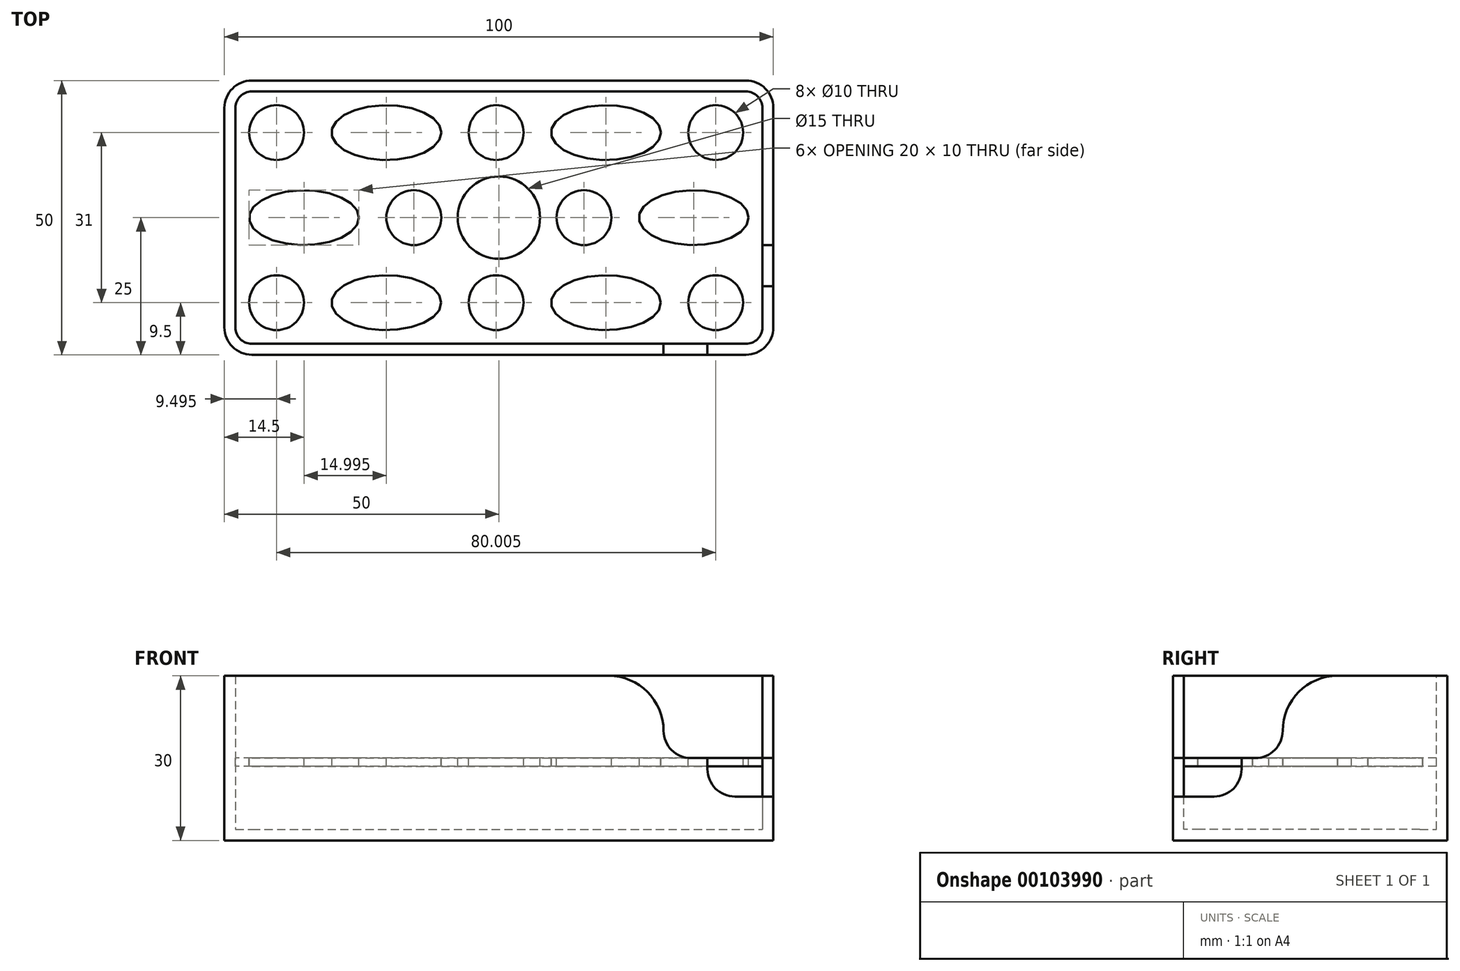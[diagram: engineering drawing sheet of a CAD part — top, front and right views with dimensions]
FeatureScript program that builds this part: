
annotation { "Feature Type Name" : "Feature", "Feature Type Description" : "" }
export const myFeature = defineFeature(function(context is Context, id is Id, definition is map)
    precondition{}
    {
        {
            var Q0;
            Q0=qCreatedBy(makeId("Top.planeOp"),FACE);
            var sketch = newSketch(context, id + "F0", { "sketchPlane" : qUnion([Q0])});
            skLineSegment(sketch, "E0.bottom", {"start": v(-50, 25) * mm, "end": v(50, 25) * mm});
            skLineSegment(sketch, "E0.top", {"start": v(-50, -25) * mm, "end": v(50, -25) * mm});
            skLineSegment(sketch, "E0.left", {"start": v(-50, 25) * mm, "end": v(-50, -25) * mm});
            skLineSegment(sketch, "E0.right", {"start": v(50, 25) * mm, "end": v(50, -25) * mm});
            skSolve(sketch);
        }
        {
            var Q0;
            Q0=makeQuery(id+"F0.imprint","IMPRINT",FACE,{"disambiguationData":[TD([[makeQuery(id+"F0.imprint","IMPRINT",EDGE,{"derivedFrom":sQuery(id+"F0.wireOp",EDGE,"E0.bottom")}),-1.0]])]});
            extrude(context, id + "F1", {"entities" : qUnion([Q0]), "depth" : 30 * mm});
        }
        {
            var Q0;
            Q0=makeQuery(id+"F1.opExtrude","SWEPT_EDGE",EDGE,{"disambiguationData":[OSD([sQuery(id+"F0.wireOp",EDGE,"E0.top"),sQuery(id+"F0.wireOp",EDGE,"E0.right")])]});
            var Q1;
            Q1=makeQuery(id+"F1.opExtrude","SWEPT_EDGE",EDGE,{"disambiguationData":[OSD([sQuery(id+"F0.wireOp",EDGE,"E0.bottom"),sQuery(id+"F0.wireOp",EDGE,"E0.right")])]});
            var Q2;
            Q2=makeQuery(id+"F1.opExtrude","SWEPT_EDGE",EDGE,{"disambiguationData":[OSD([sQuery(id+"F0.wireOp",EDGE,"E0.top"),sQuery(id+"F0.wireOp",EDGE,"E0.left")])]});
            var Q3;
            Q3=makeQuery(id+"F1.opExtrude","SWEPT_EDGE",EDGE,{"disambiguationData":[OSD([sQuery(id+"F0.wireOp",EDGE,"E0.bottom"),sQuery(id+"F0.wireOp",EDGE,"E0.left")])]});
            fillet(context, id + "F2", {"entities" : qUnion([Q0, Q1, Q2, Q3]), "radius" : 5 * mm, "tangentPropagation" : true, "allowEdgeOverflow" : false});
        }
        {
            var Q0;
            Q0=makeQuery(id+"F1.opExtrude","CAP_FACE",FACE,{"disambiguationData":[OSD([sQuery(id+"F0.wireOp",EDGE,"E0.bottom"),sQuery(id+"F0.wireOp",EDGE,"E0.top"),sQuery(id+"F0.wireOp",EDGE,"E0.left"),sQuery(id+"F0.wireOp",EDGE,"E0.right")])],"isStart":false});
            shell(context, id + "F3", {"entities" : qUnion([Q0]), "thickness" : 2 * mm});
        }
        {
            var Q0;
            Q0=makeQuery(id+"F1.opExtrude","SWEPT_FACE",FACE,{"disambiguationData":[OSD([sQuery(id+"F0.wireOp",EDGE,"E0.top")])]});
            var sketch = newSketch(context, id + "F4", { "sketchPlane" : qUnion([Q0])});
            skLineSegment(sketch, "E1.bottom", {"start": v(30, 15) * mm, "end": v(56.02, 15) * mm});
            skLineSegment(sketch, "E1.top", {"start": v(30, 39.69) * mm, "end": v(56.02, 39.69) * mm});
            skLineSegment(sketch, "E1.left", {"start": v(30, 15) * mm, "end": v(30, 39.69) * mm});
            skLineSegment(sketch, "E1.right", {"start": v(56.02, 15) * mm, "end": v(56.02, 39.69) * mm});
            skSolve(sketch);
        }
        {
            var Q0;
            {var subQ0=sQuery(id+"F4.wireOp",EDGE,"E1.left");var subQ1=sQuery(id+"F4.wireOp",EDGE,"E1.bottom");var subQ2=makeQuery(id+"F4.imprint","INTERSECT",VERTEX,{"derivedFrom":[subQ1,subQ0]});Q0=makeQuery(id+"F4.imprint","IMPRINT",FACE,{"disambiguationData":[TD([[makeQuery(id+"F4.imprint","IMPRINT",EDGE,{"disambiguationData":[TD([[subQ2,-1.0]])],"derivedFrom":subQ0}),-1.0]])]});}
            var Q1;
            {var subQ1=sQuery(id+"F4.wireOp",EDGE,"E1.top");Q1=makeQuery(id+"F4.imprint","IMPRINT",FACE,{"disambiguationData":[TD([[makeQuery(id+"F4.imprint","IMPRINT",EDGE,{"derivedFrom":subQ1}),-1.0]])]});}
            extrude(context, id + "F5", {"entities" : qUnion([Q0, Q1]), "operationType" : NewBodyOperationType.REMOVE, "oppositeDirection" : true, "depth" : 20 * mm});
        }
        {
            var Q0;
            Q0=makeQuery(id+"F1.opExtrude","SWEPT_FACE",FACE,{"disambiguationData":[OSD([sQuery(id+"F0.wireOp",EDGE,"E0.top")])]});
            var sketch = newSketch(context, id + "F6", { "sketchPlane" : qUnion([Q0])});
            skLineSegment(sketch, "E2.bottom", {"start": v(38, 18.82) * mm, "end": v(56.92, 18.82) * mm});
            skLineSegment(sketch, "E2.top", {"start": v(38, 8) * mm, "end": v(56.92, 8) * mm});
            skLineSegment(sketch, "E2.left", {"start": v(38, 18.82) * mm, "end": v(38, 8) * mm});
            skLineSegment(sketch, "E2.right", {"start": v(56.92, 18.82) * mm, "end": v(56.92, 8) * mm});
            skSolve(sketch);
        }
        {
            var Q0;
            {var subQ0=sQuery(id+"F6.wireOp",EDGE,"E2.left");var subQ1=sQuery(id+"F6.wireOp",EDGE,"E2.top");var subQ2=makeQuery(id+"F6.imprint","INTERSECT",VERTEX,{"derivedFrom":[subQ1,subQ0]});Q0=makeQuery(id+"F6.imprint","IMPRINT",FACE,{"disambiguationData":[TD([[makeQuery(id+"F6.imprint","IMPRINT",EDGE,{"disambiguationData":[TD([[subQ2,1.0]])],"derivedFrom":subQ0}),1.0]])]});}
            var Q1;
            {var subQ2=sQuery(id+"F6.wireOp",EDGE,"E2.bottom");Q1=makeQuery(id+"F6.imprint","IMPRINT",FACE,{"disambiguationData":[TD([[makeQuery(id+"F6.imprint","IMPRINT",EDGE,{"derivedFrom":subQ2}),-1.0]])]});}
            extrude(context, id + "F7", {"entities" : qUnion([Q0, Q1]), "operationType" : NewBodyOperationType.REMOVE, "oppositeDirection" : true, "depth" : 12.5 * mm});
        }
        {
            var Q0;
            Q0=qCreatedBy(makeId("Top.planeOp"),FACE);
            cPlane(context, id + "F8", {"entities" : qUnion([Q0]), "cplaneType" : CPlaneType.OFFSET, "offset" : 15 * mm, "width" : 150 * mm, "height" : 150 * mm});
        }
        {
            var Q0;
            Q0=qCreatedBy(id+"F8.planeOp",FACE);
            var sketch = newSketch(context, id + "F9", { "sketchPlane" : qUnion([Q0])});
            skCircle(sketch, "E3", {"center": v(-40.5, 15.5) * mm, "radius": 5 * mm});
            skEllipse(sketch, "E4", {"center": v(-20.5, 15.5) * mm, "majorRadius": 10 * mm, "minorRadius": 5 * mm, "majorAxis": v(1, 0)});
            skEllipse(sketch, "E5.1.0.0", {"center": v(19.5, 15.5) * mm, "majorRadius": 10 * mm, "minorRadius": 5 * mm, "majorAxis": v(1, 0)});
            skCircle(sketch, "E5.1.0.1", {"center": v(-0.5, 15.5) * mm, "radius": 5 * mm});
            skCircle(sketch, "E5.2.0.1", {"center": v(39.5, 15.5) * mm, "radius": 5 * mm});
            skLineSegment(sketch, "E5.direction1", {"start": v(-20.5, 15.5) * mm, "end": v(19.5, 15.5) * mm, "construction": true});
            skEllipse(sketch, "E6", {"center": v(-35.5, 0) * mm, "majorRadius": 10 * mm, "minorRadius": 5 * mm, "majorAxis": v(1, 0)});
            skCircle(sketch, "E7.1.0.1", {"center": v(-15.5, 0) * mm, "radius": 5 * mm});
            skEllipse(sketch, "E8", {"center": v(35.5, 0) * mm, "majorRadius": 10 * mm, "minorRadius": 5 * mm, "majorAxis": v(1, 0)});
            skCircle(sketch, "E9.1.0.1", {"center": v(15.5, 0) * mm, "radius": 5 * mm});
            skCircle(sketch, "E10.1.0.0", {"center": v(-40.5, -15.5) * mm, "radius": 5 * mm});
            skEllipse(sketch, "E10.1.0.1", {"center": v(-20.5, -15.5) * mm, "majorRadius": 10 * mm, "minorRadius": 5 * mm, "majorAxis": v(1, 0)});
            skCircle(sketch, "E10.1.0.2", {"center": v(-0.5, -15.5) * mm, "radius": 5 * mm});
            skEllipse(sketch, "E10.1.0.3", {"center": v(19.5, -15.5) * mm, "majorRadius": 10 * mm, "minorRadius": 5 * mm, "majorAxis": v(1, 0)});
            skCircle(sketch, "E10.1.0.4", {"center": v(39.5, -15.5) * mm, "radius": 5 * mm});
            skLineSegment(sketch, "E10.direction1", {"start": v(-40.5, 15.5) * mm, "end": v(-40.5, -15.5) * mm, "construction": true});
            skCircle(sketch, "E11", {"center": v(0, 0) * mm, "radius": 7.5 * mm});
            skSolve(sketch);
        }
        {
            var Q0;
            Q0=qCreatedBy(id+"F8.planeOp",FACE);
            var sketch = newSketch(context, id + "F10", { "sketchPlane" : qUnion([Q0])});
            skLineSegment(sketch, "E12.0.0", {"start": v(-48, 20) * mm, "end": v(-48, -20) * mm});
            skArc(sketch, "E12.0.1", {"start": v(-45, -23) * mm, "mid": v(-47.12, -22.12) * mm, "end": v(-48, -20) * mm});
            skLineSegment(sketch, "E12.0.2", {"start": v(-45, -23) * mm, "end": v(45, -23) * mm});
            skArc(sketch, "E12.0.3", {"start": v(48, -20) * mm, "mid": v(47.12, -22.12) * mm, "end": v(45, -23) * mm});
            skLineSegment(sketch, "E12.0.4", {"start": v(48, -20) * mm, "end": v(48, 20) * mm});
            skArc(sketch, "E12.0.5", {"start": v(45, 23) * mm, "mid": v(47.12, 22.12) * mm, "end": v(48, 20) * mm});
            skLineSegment(sketch, "E12.0.6", {"start": v(45, 23) * mm, "end": v(-45, 23) * mm});
            skArc(sketch, "E12.0.7", {"start": v(-48, 20) * mm, "mid": v(-47.12, 22.12) * mm, "end": v(-45, 23) * mm});
            skSolve(sketch);
        }
        {
            var Q0;
            Q0=makeQuery(id+"F10.imprint","IMPRINT",FACE,{"disambiguationData":[TD([[makeQuery(id+"F10.imprint","IMPRINT",EDGE,{"derivedFrom":sQuery(id+"F10.wireOp",EDGE,"E12.0.0")}),1.0]])]});
            var Q1;
            Q1 = qConstructionFilter(qBodyType(qCreatedBy(id + "F10" ,EDGE), BodyType.WIRE), ConstructionObject.NO);
            extrude(context, id + "F11", {"entities" : qUnion([Q0]), "surfaceEntities" : qUnion([Q1]), "oppositeDirection" : true, "depth" : 1.5 * mm});
        }
        {
            var Q0;
            Q0 = qSketchRegion(id + "F9", true);
            extrude(context, id + "F12", {"entities" : qUnion([Q0]), "operationType" : NewBodyOperationType.REMOVE, "oppositeDirection" : true, "depth" : 3 * mm});
        }
        {
            var Q0;
            Q0=makeQuery(id+"F5.boolean.opBoolean","INTERSECT",EDGE,{"derivedFrom":[makeQuery(id+"F1.opExtrude","CAP_FACE",FACE,{"disambiguationData":[OSD([sQuery(id+"F0.wireOp",EDGE,"E0.bottom"),sQuery(id+"F0.wireOp",EDGE,"E0.top"),sQuery(id+"F0.wireOp",EDGE,"E0.left"),sQuery(id+"F0.wireOp",EDGE,"E0.right")])],"isStart":false}),makeQuery(id+"F5.opExtrude","SWEPT_FACE",FACE,{"disambiguationData":[OSD([sQuery(id+"F4.wireOp",EDGE,"E1.left")])]})]});
            var Q1;
            Q1=makeQuery(id+"F5.boolean.opBoolean","INTERSECT",EDGE,{"derivedFrom":[makeQuery(id+"F1.opExtrude","CAP_FACE",FACE,{"disambiguationData":[OSD([sQuery(id+"F0.wireOp",EDGE,"E0.bottom"),sQuery(id+"F0.wireOp",EDGE,"E0.top"),sQuery(id+"F0.wireOp",EDGE,"E0.left"),sQuery(id+"F0.wireOp",EDGE,"E0.right")])],"isStart":false}),makeQuery(id+"F5.opExtrude","CAP_FACE",FACE,{"disambiguationData":[OSD([sQuery(id+"F4.wireOp",EDGE,"E1.bottom"),sQuery(id+"F4.wireOp",EDGE,"E1.top"),sQuery(id+"F4.wireOp",EDGE,"E1.left"),sQuery(id+"F4.wireOp",EDGE,"E1.right")])],"isStart":false})]});
            fillet(context, id + "F13", {"entities" : qUnion([Q0, Q1]), "radius" : 10 * mm, "tangentPropagation" : true, "allowEdgeOverflow" : false});
        }
        {
            var Q0;
            Q0=makeQuery(id+"F5.boolean.opBoolean","COPY",EDGE,{"derivedFrom":makeQuery(id+"F5.opExtrude","SWEPT_EDGE",EDGE,{"disambiguationData":[OSD([sQuery(id+"F4.wireOp",EDGE,"E1.bottom"),sQuery(id+"F4.wireOp",EDGE,"E1.left")])]})});
            var Q1;
            Q1=makeQuery(id+"F5.boolean.opBoolean","COPY",EDGE,{"derivedFrom":makeQuery(id+"F5.opExtrude","CAP_EDGE",EDGE,{"disambiguationData":[OSD([sQuery(id+"F4.wireOp",EDGE,"E1.bottom")])],"isStart":false})});
            fillet(context, id + "F14", {"entities" : qUnion([Q0, Q1]), "radius" : 5 * mm, "tangentPropagation" : true, "allowEdgeOverflow" : false});
        }
        {
            var Q0;
            Q0=makeQuery(id+"F7.boolean.opBoolean","COPY",EDGE,{"derivedFrom":makeQuery(id+"F7.opExtrude","SWEPT_EDGE",EDGE,{"disambiguationData":[OSD([sQuery(id+"F6.wireOp",EDGE,"E2.top"),sQuery(id+"F6.wireOp",EDGE,"E2.left")])]})});
            var Q1;
            Q1=makeQuery(id+"F7.boolean.opBoolean","COPY",EDGE,{"derivedFrom":makeQuery(id+"F7.opExtrude","CAP_EDGE",EDGE,{"disambiguationData":[OSD([sQuery(id+"F6.wireOp",EDGE,"E2.top")])],"isStart":false})});
            fillet(context, id + "F15", {"entities" : qUnion([Q0, Q1]), "radius" : 5 * mm, "tangentPropagation" : true, "allowEdgeOverflow" : false});
        }
    });
